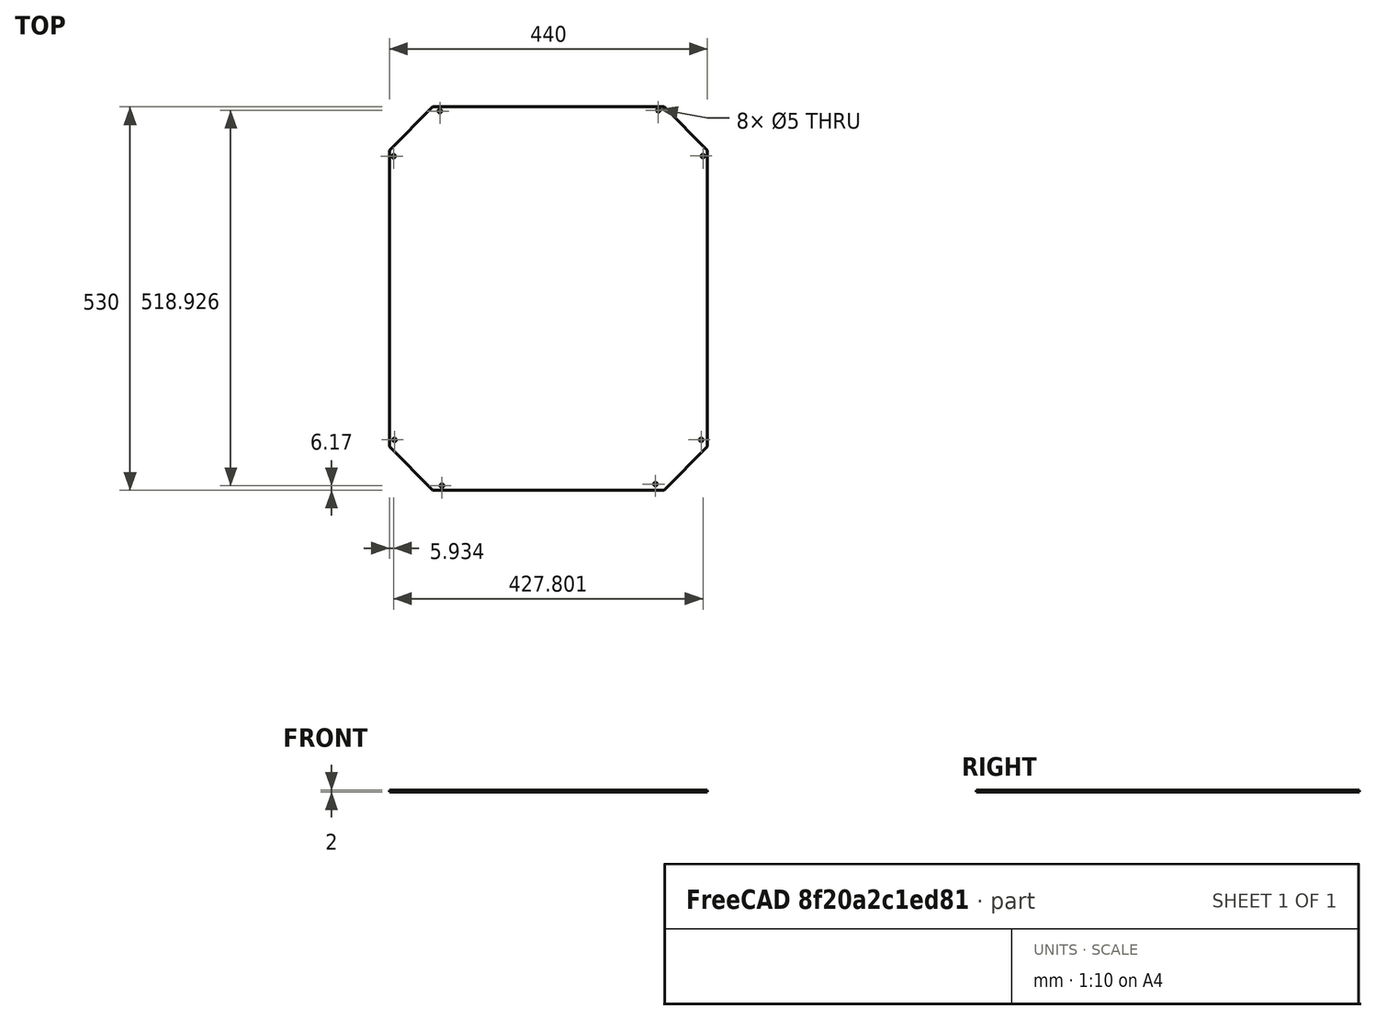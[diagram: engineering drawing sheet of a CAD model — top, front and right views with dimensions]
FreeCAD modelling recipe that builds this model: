
FCSTD DOCUMENT  (FreeCAD 0.16R6698 (Git))
Label: Plaque peau serveur equerre
License: All rights reserved
LicenseURL: http://en.wikipedia.org/wiki/All_rights_reserved
objects: Sketcher::SketchObject×1, PartDesign::Pad×1
note: 3 computed .brp shape members not serialized (recipe doc carries the construction recipe); baked Part::Feature solids carry a one-line shape summary decoded from their .brp

FEATURE [Sketcher::SketchObject] Sketch
  sketch-geometry (16):
    g0: LineSegment StartX=-166.364 StartY=259.917 StartZ=0 EndX=153.636 EndY=259.917 EndZ=0
    g1: LineSegment StartX=153.636 StartY=259.917 StartZ=0 EndX=213.636 EndY=199.917 EndZ=0
    g2: LineSegment StartX=213.636 StartY=199.917 StartZ=0 EndX=213.636 EndY=-210.083 EndZ=0
    g3: LineSegment StartX=213.636 StartY=-210.083 StartZ=0 EndX=153.636 EndY=-270.083 EndZ=0
    g4: LineSegment StartX=153.636 StartY=-270.083 StartZ=0 EndX=-166.364 EndY=-270.083 EndZ=0
    g5: LineSegment StartX=-166.364 StartY=-270.083 StartZ=0 EndX=-226.364 EndY=-210.083 EndZ=0
    g6: LineSegment StartX=-226.364 StartY=-210.083 StartZ=0 EndX=-226.364 EndY=199.917 EndZ=0
    g7: LineSegment StartX=-226.364 StartY=199.917 StartZ=0 EndX=-166.364 EndY=259.917 EndZ=0
    g8: Circle CenterX=-220.426 CenterY=191.552 CenterZ=0 NormalX=0 NormalY=0 NormalZ=1 Radius=2.5
    g9: Circle CenterX=-156.405 CenterY=253.931 CenterZ=0 NormalX=0 NormalY=0 NormalZ=1 Radius=2.5
    g10: Circle CenterX=145.683 CenterY=255.016 CenterZ=0 NormalX=0 NormalY=0 NormalZ=1 Radius=2.5
    g11: Circle CenterX=-219.195 CenterY=-200.608 CenterZ=0 NormalX=0 NormalY=0 NormalZ=1 Radius=2.5
    g12: Circle CenterX=-153.602 CenterY=-263.91 CenterZ=0 NormalX=0 NormalY=0 NormalZ=1 Radius=2.5
    g13: Circle CenterX=141.603 CenterY=-261.7 CenterZ=0 NormalX=0 NormalY=0 NormalZ=1 Radius=2.5
    g14: Circle CenterX=204.926 CenterY=-200.477 CenterZ=0 NormalX=0 NormalY=0 NormalZ=1 Radius=2.5
    g15: Circle CenterX=207.375 CenterY=191.908 CenterZ=0 NormalX=0 NormalY=0 NormalZ=1 Radius=2.5
  constraints (27):
    c: Horizontal(g0)
    c: Coincident(g0,g1)
    c: Coincident(g1,g2)
    c: Vertical(g2)
    c: Coincident(g2,g3)
    c: Coincident(g3,g4)
    c: Horizontal(g4)
    c: Coincident(g4,g5)
    c: Coincident(g5,g6)
    c: Vertical(g6)
    c: Coincident(g6,g7)
    c: Coincident(g7,g0)
    c: DistanceY(g7,g7) = 60
    c: DistanceX(g1,g1) = 60
    c: DistanceX(g5,g5) = 60
    c: DistanceY(g5,g5) = 60
    c: DistanceY(g3,g3) = 60
    c: DistanceY(g1,g1) = 60
    c: DistanceX(g3,g3) = 60
    c: Radius(g15) = 2.5
    c: Equal(g15,g10)
    c: Equal(g15,g9)
    c: Equal(g15,g8)
    c: Equal(g15, g11-g14) x4
    c: DistanceX(g6,g0) = 60
    c: DistanceX(g0,g0) = 320
    c: DistanceY(g6,g6) = 410
FEATURE [PartDesign::Pad] Pad
  Length = 2
  Length2 = 100
  Sketch = -> Sketch
  Type = 0
